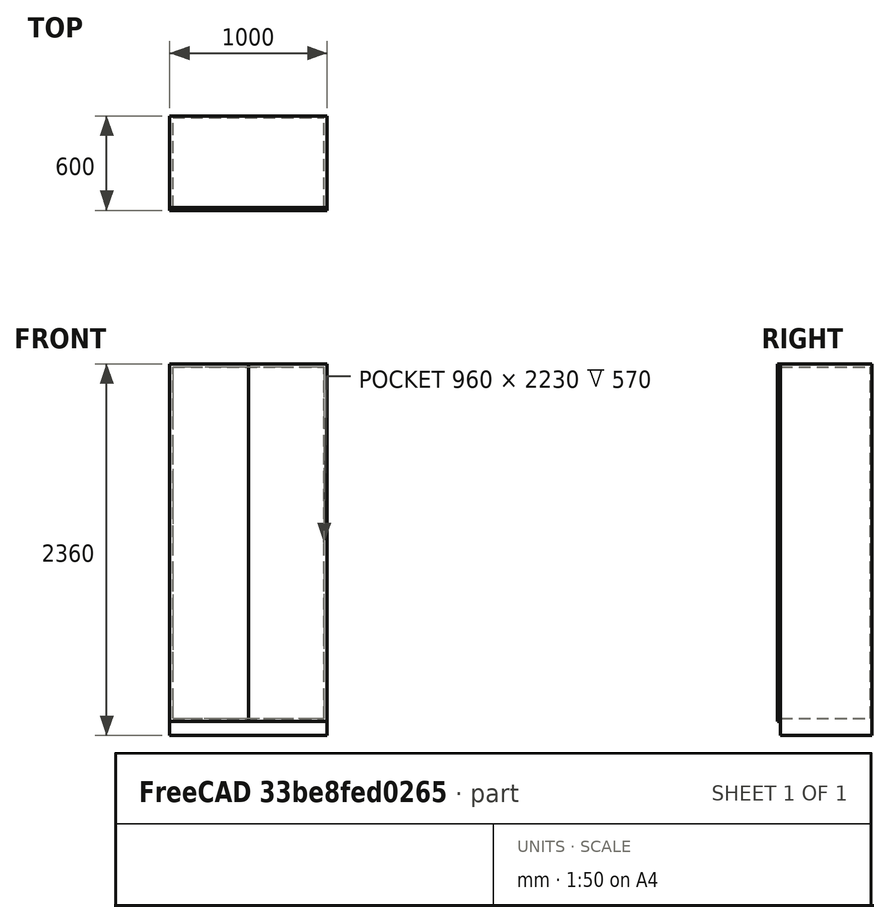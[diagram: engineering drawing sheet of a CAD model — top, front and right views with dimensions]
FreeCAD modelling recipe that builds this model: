
FCSTD DOCUMENT  (FreeCAD 0.19R20036 (Git))
Label: Parametric Cabinet
License: All rights reserved
LicenseURL: http://en.wikipedia.org/wiki/All_rights_reserved
objects: Part::Box×3, App::FeaturePython×1, Part::Cut×1, Part::FeaturePython×1, App::Part×1
note: 5 computed .brp shape members not serialized (recipe doc carries the construction recipe); baked Part::Feature solids carry a one-line shape summary decoded from their .brp

FEATURE [Part::Box] Box  label="Cubo"
  AttacherType = Attacher::AttachEngine3D
  Height = 2360
  Length = 1000
  Placement = pos=(-500,-580,0) rot=(0,0,1;0rad)
  Width = 580
  expr: Length = dd.ddLength
  expr: Width = dd.ddWidth
  expr: Height = dd.ddHeight
  expr: .Placement.Base.x = -dd.ddLength / 2
  expr: .Placement.Base.y = -dd.ddWidth
FEATURE [App::FeaturePython] dd  label="Dimensions"  # WARN: FeaturePython — macro-defined, semantics opaque (R4)
  DynamicData = Created with DynamicData (v1.76) workbench. | This is a simple container object built | for holding custom properties.  Worbench | installation is not required to use the | container object -- instead only for | adding / removing custom properties. | (But this can also be done via scripting.)
  ddHeight = 2360
  ddLength = 1000
  ddN_of_doors = 2
  ddPlith = 90
  ddVisibleDoors = false
  ddWidth = 580
FEATURE [Part::Box] Box002  label="Cubo002"
  AttacherType = Attacher::AttachEngine3D
  Height = 2230
  Length = 960
  Placement = pos=(-480,-580,110) rot=(0,0,1;0rad)
  Width = 570
  expr: .Placement.Base.z = dd.ddPlith + 0.02m
  expr: Length = dd.ddLength - 0.04m
  expr: Width = dd.ddWidth - 0.01m
  expr: Height = dd.ddHeight - dd.ddPlith - 40mm
  expr: .Placement.Base.y = -dd.ddWidth
  expr: .Placement.Base.x = -(dd.ddLength - 4cm) / 2
FEATURE [Part::Cut] Cut  label="Cabinet stucture"
  Base = -> Box
  Refine = true
  Tool = -> Box002
FEATURE [Part::Box] Box003  label="Door"
  AttacherType = Attacher::AttachEngine3D
  Height = 2270
  Length = 500
  Placement = pos=(-500,-600,90) rot=(0,0,1;0rad)
  Width = 20
  expr: .Placement.Base.z = dd.ddPlith
  expr: Height = dd.ddHeight - dd.ddPlith
  expr: Length = dd.ddLength / dd.ddN_of_doors
  expr: .Placement.Base.x = -dd.ddLength / 2
  expr: .Placement.Base.y = -dd.ddWidth - 20mm
FEATURE [Part::FeaturePython] Array  label="Doors"  # Draft array (typed FeaturePython)
  Angle = 360
  ArrayType = 0
  Axis = (0,0,1)
  Base = -> Box003
  Center = (0,0,0)
  Fuse = false
  IntervalAxis = (0,0,0)
  IntervalX = (500,0,0)
  IntervalY = (0,100,0)
  IntervalZ = (0,0,100)
  NumberCircles = 1
  NumberPolar = 1
  NumberX = 2
  NumberY = 1
  NumberZ = 1
  RadialDistance = 1
  Symmetry = 1
  TangentialDistance = 1
  expr: NumberX = dd.ddN_of_doors
  expr: .IntervalX.x = dd.ddLength / dd.ddN_of_doors
FEATURE [App::Part] Part  label="Cabinet"
  Group = -> [Box,dd,Box002,Cut,Box003,Array]
  Origin = -> Origin
